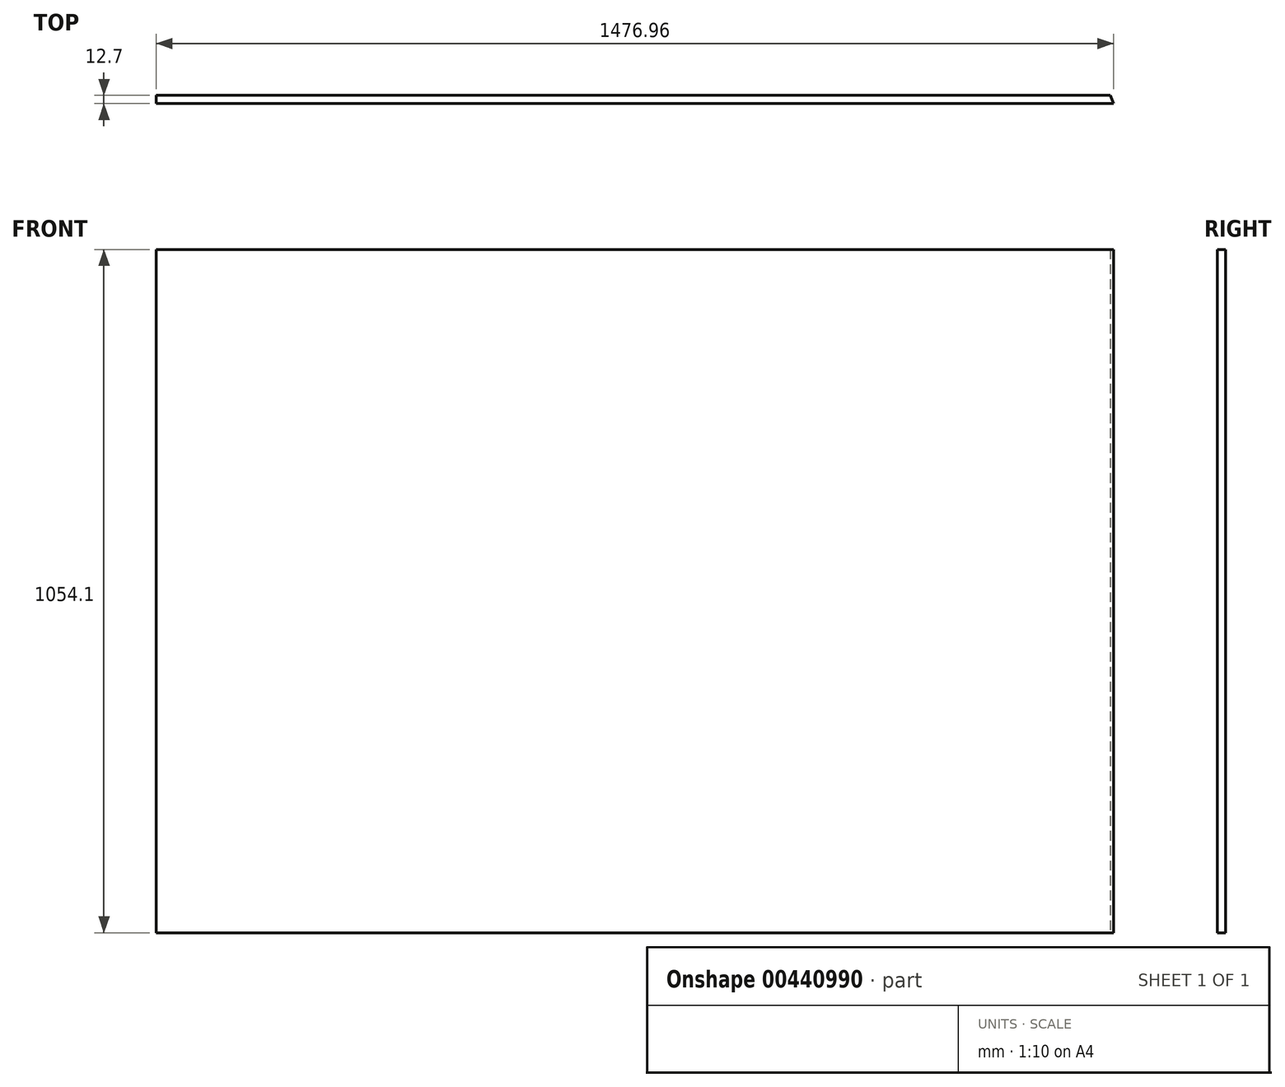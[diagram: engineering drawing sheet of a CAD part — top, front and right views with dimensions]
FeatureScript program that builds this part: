
annotation { "Feature Type Name" : "Feature", "Feature Type Description" : "" }
export const myFeature = defineFeature(function(context is Context, id is Id, definition is map)
    precondition{}
    {
        {
            var Q0;
            Q0=qCreatedBy(makeId("Front.planeOp"),FACE);
            var sketch = newSketch(context, id + "F0", { "sketchPlane" : qUnion([Q0])});
            skLineSegment(sketch, "E0.bottom", {"start": v(0, 0) * mm, "end": v(1476.96, 0) * mm});
            skLineSegment(sketch, "E0.top", {"start": v(0, 1054.1) * mm, "end": v(1476.96, 1054.1) * mm});
            skLineSegment(sketch, "E0.left", {"start": v(0, 0) * mm, "end": v(0, 1054.1) * mm});
            skLineSegment(sketch, "E0.right", {"start": v(1476.96, 0) * mm, "end": v(1476.96, 1054.1) * mm});
            skSolve(sketch);
        }
        {
            var Q0;
            Q0=makeQuery(id+"F0.imprint","IMPRINT",FACE,{"disambiguationData":[TD([[makeQuery(id+"F0.imprint","IMPRINT",EDGE,{"derivedFrom":sQuery(id+"F0.wireOp",EDGE,"E0.bottom")}),1.0]])]});
            extrude(context, id + "F1", {"entities" : qUnion([Q0]), "oppositeDirection" : true, "depth" : 12.7 * mm});
        }
        {
            var Q0;
            Q0=makeQuery(id+"F1.opExtrude","CAP_EDGE",EDGE,{"disambiguationData":[OSD([sQuery(id+"F0.wireOp",EDGE,"E0.right")])],"isStart":false});
            chamfer(context, id + "F2", {"entities" : qUnion([Q0]), "chamferType" : ChamferType.OFFSET_ANGLE, "width" : 12.7 * mm, "oppositeDirection" : false, "angle" : 22.5 * degree, "tangentPropagation" : true});
        }
    });
